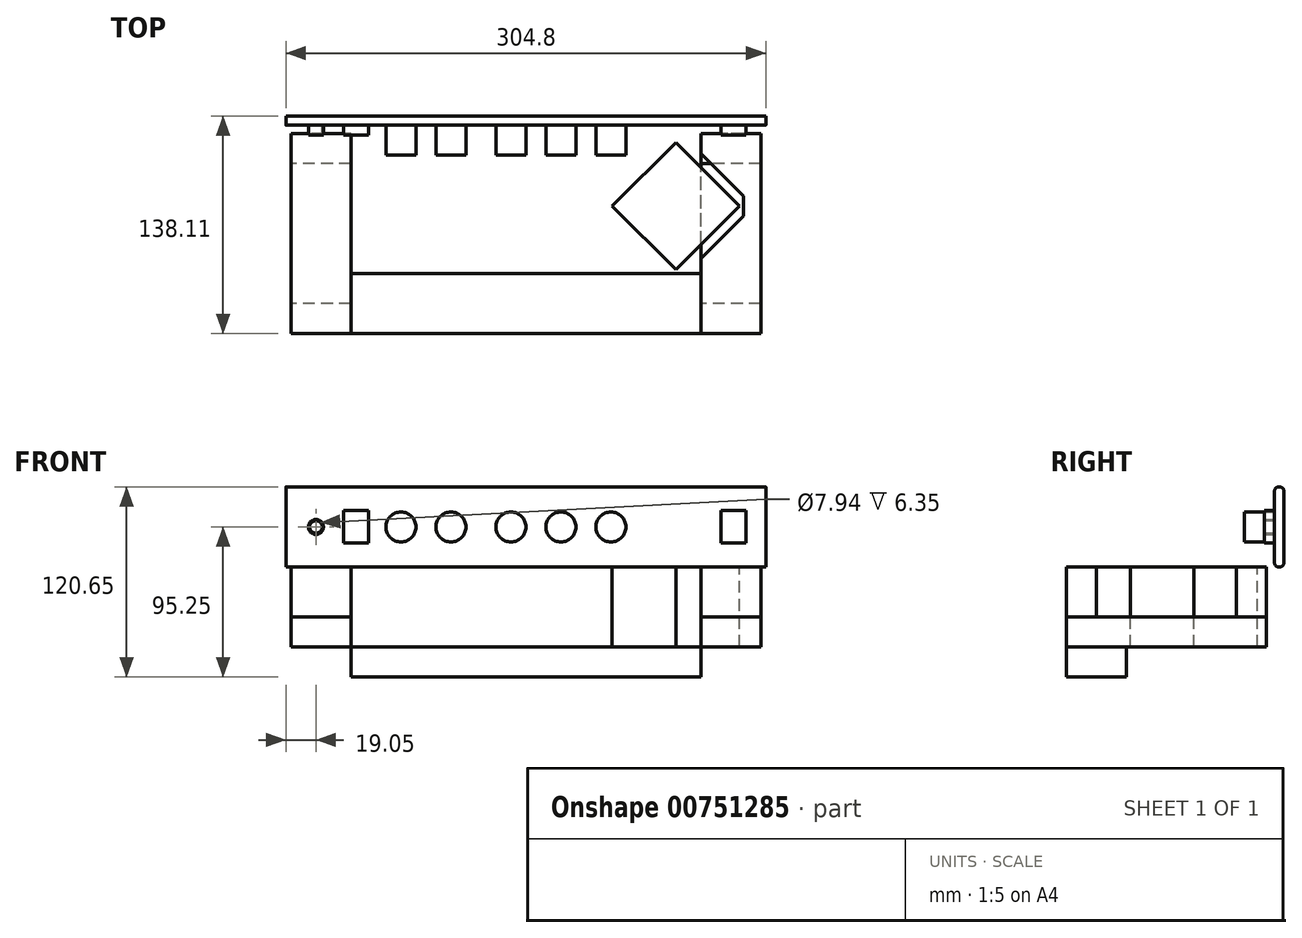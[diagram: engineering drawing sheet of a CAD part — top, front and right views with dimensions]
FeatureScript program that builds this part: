
annotation { "Feature Type Name" : "Feature", "Feature Type Description" : "" }
export const myFeature = defineFeature(function(context is Context, id is Id, definition is map)
    precondition{}
    {
        {
            var Q0;
            Q0=qCreatedBy(makeId("Front.planeOp"),FACE);
            var sketch = newSketch(context, id + "F0", { "sketchPlane" : qUnion([Q0])});
            skLineSegment(sketch, "E0.bottom", {"start": v(152.4, 25.4) * mm, "end": v(-152.4, 25.4) * mm});
            skLineSegment(sketch, "E0.top", {"start": v(152.4, -25.4) * mm, "end": v(-152.4, -25.4) * mm});
            skLineSegment(sketch, "E0.left", {"start": v(152.4, 25.4) * mm, "end": v(152.4, -25.4) * mm});
            skLineSegment(sketch, "E0.right", {"start": v(-152.4, 25.4) * mm, "end": v(-152.4, -25.4) * mm});
            skPoint(sketch, "E0.middle", {"position": v(0, 0) * mm});
            skSolve(sketch);
        }
        {
            var Q0;
            Q0=makeQuery(id+"F0.imprint","IMPRINT",FACE,{"disambiguationData":[TD([[makeQuery(id+"F0.imprint","IMPRINT",EDGE,{"derivedFrom":sQuery(id+"F0.wireOp",EDGE,"E0.bottom")}),1.0]])]});
            extrude(context, id + "F1", {"entities" : qUnion([Q0]), "depth" : (5 + (7 / 8)) * mm, "offsetDistance" : 25.4 * mm});
        }
        {
            var Q0;
            Q0=makeQuery(id+"F1.opExtrude","CAP_FACE",FACE,{"disambiguationData":[OSD([sQuery(id+"F0.wireOp",EDGE,"E0.bottom"),sQuery(id+"F0.wireOp",EDGE,"E0.top"),sQuery(id+"F0.wireOp",EDGE,"E0.left"),sQuery(id+"F0.wireOp",EDGE,"E0.right")])],"isStart":false});
            cPlane(context, id + "F2", {"entities" : qUnion([Q0]), "cplaneType" : CPlaneType.OFFSET, "offset" : 0 * mm, "width" : 152.4 * mm, "height" : 152.4 * mm});
        }
        {
            var Q0;
            Q0=qCreatedBy(id+"F2.planeOp",FACE);
            var sketch = newSketch(context, id + "F3", { "sketchPlane" : qUnion([Q0])});
            skCircle(sketch, "E1", {"center": v(-133.35, 0) * mm, "radius": 4.76 * mm});
            skCircle(sketch, "E2", {"center": v(-133.35, 0) * mm, "radius": 3.97 * mm});
            skLineSegment(sketch, "E3.bottom", {"start": v(-100.01, 10.32) * mm, "end": v(-115.89, 10.32) * mm});
            skLineSegment(sketch, "E3.top", {"start": v(-100.01, -10.32) * mm, "end": v(-115.89, -10.32) * mm});
            skLineSegment(sketch, "E3.left", {"start": v(-100.01, 10.32) * mm, "end": v(-100.01, -10.32) * mm});
            skLineSegment(sketch, "E3.right", {"start": v(-115.89, 10.32) * mm, "end": v(-115.89, -10.32) * mm});
            skPoint(sketch, "E3.middle", {"position": v(-107.95, 0) * mm});
            skLineSegment(sketch, "E4.bottom", {"start": v(139.7, 10.32) * mm, "end": v(123.83, 10.32) * mm});
            skLineSegment(sketch, "E4.top", {"start": v(139.7, -10.32) * mm, "end": v(123.83, -10.32) * mm});
            skLineSegment(sketch, "E4.left", {"start": v(139.7, 10.32) * mm, "end": v(139.7, -10.32) * mm});
            skLineSegment(sketch, "E4.right", {"start": v(123.83, 10.32) * mm, "end": v(123.83, -10.32) * mm});
            skPoint(sketch, "E4.middle", {"position": v(131.76, 0) * mm});
            skSolve(sketch);
        }
        {
            var Q0;
            Q0=qSketchRegion(id+"F3",true);
            extrude(context, id + "F4", {"entities" : qUnion([Q0]), "operationType" : NewBodyOperationType.ADD, "depth" : 6.35 * mm, "offsetDistance" : 25.4 * mm});
        }
        {
            var Q0;
            Q0=qCreatedBy(id+"F2.planeOp",FACE);
            var sketch = newSketch(context, id + "F5", { "sketchPlane" : qUnion([Q0])});
            skCircle(sketch, "E5", {"center": v(-79.38, 0) * mm, "radius": 9.53 * mm});
            skCircle(sketch, "E6", {"center": v(-47.62, 0) * mm, "radius": 9.53 * mm});
            skCircle(sketch, "E7", {"center": v(-9.52, 0) * mm, "radius": 9.53 * mm});
            skCircle(sketch, "E8", {"center": v(22.23, 0) * mm, "radius": 9.53 * mm});
            skCircle(sketch, "E9", {"center": v(53.98, 0) * mm, "radius": 9.53 * mm});
            skSolve(sketch);
        }
        {
            var Q0;
            Q0=makeQuery(id+"F5.imprint","IMPRINT",FACE,{"disambiguationData":[TD([[makeQuery(id+"F5.imprint","IMPRINT",EDGE,{"derivedFrom":sQuery(id+"F5.wireOp",EDGE,"E5")}),1.0]])]});
            var Q1;
            Q1=makeQuery(id+"F5.imprint","IMPRINT",FACE,{"disambiguationData":[TD([[makeQuery(id+"F5.imprint","IMPRINT",EDGE,{"derivedFrom":sQuery(id+"F5.wireOp",EDGE,"E6")}),1.0]])]});
            var Q2;
            Q2=makeQuery(id+"F5.imprint","IMPRINT",FACE,{"disambiguationData":[TD([[makeQuery(id+"F5.imprint","IMPRINT",EDGE,{"derivedFrom":sQuery(id+"F5.wireOp",EDGE,"E7")}),1.0]])]});
            var Q3;
            Q3=makeQuery(id+"F5.imprint","IMPRINT",FACE,{"disambiguationData":[TD([[makeQuery(id+"F5.imprint","IMPRINT",EDGE,{"derivedFrom":sQuery(id+"F5.wireOp",EDGE,"E8")}),1.0]])]});
            var Q4;
            Q4=makeQuery(id+"F5.imprint","IMPRINT",FACE,{"disambiguationData":[TD([[makeQuery(id+"F5.imprint","IMPRINT",EDGE,{"derivedFrom":sQuery(id+"F5.wireOp",EDGE,"E9")}),1.0]])]});
            extrude(context, id + "F6", {"entities" : qUnion([Q0, Q1, Q2, Q3, Q4]), "operationType" : NewBodyOperationType.ADD, "depth" : 19.05 * mm, "offsetDistance" : 25.4 * mm});
        }
        {
            var Q0;
            Q0=makeQuery(id+"F1.opExtrude","SWEPT_FACE",FACE,{"disambiguationData":[OSD([sQuery(id+"F0.wireOp",EDGE,"E0.top")])]});
            cPlane(context, id + "F7", {"entities" : qUnion([Q0]), "cplaneType" : CPlaneType.OFFSET, "offset" : 0 * mm, "width" : 152.4 * mm, "height" : 152.4 * mm});
        }
        {
            var Q0;
            Q0=qCreatedBy(id+"F7.planeOp",FACE);
            var sketch = newSketch(context, id + "F8", { "sketchPlane" : qUnion([Q0])});
            skLineSegment(sketch, "E10.bottom", {"start": v(95.25, 16.74) * mm, "end": v(54.84, 57.15) * mm});
            skLineSegment(sketch, "E10.top", {"start": v(135.66, 57.15) * mm, "end": v(95.25, 97.56) * mm});
            skLineSegment(sketch, "E10.left", {"start": v(95.25, 16.74) * mm, "end": v(135.66, 57.15) * mm});
            skLineSegment(sketch, "E10.right", {"start": v(54.84, 57.15) * mm, "end": v(95.25, 97.56) * mm});
            skPoint(sketch, "E10.middle", {"position": v(95.25, 57.15) * mm});
            skLineSegment(sketch, "E11", {"start": v(3.18, 0) * mm, "end": v(152.4, 149.23) * mm, "construction": true});
            skSolve(sketch);
        }
        {
            var Q0;
            Q0=makeQuery(id+"F8.imprint","IMPRINT",FACE,{"disambiguationData":[TD([[makeQuery(id+"F8.imprint","IMPRINT",EDGE,{"derivedFrom":sQuery(id+"F8.wireOp",EDGE,"E10.bottom")}),-1.0]])]});
            extrude(context, id + "F9", {"entities" : qUnion([Q0]), "operationType" : NewBodyOperationType.ADD, "depth" : 50.8 * mm, "offsetDistance" : 25.4 * mm});
        }
        {
            var Q0;
            Q0=makeQuery(id+"F1.opExtrude","CAP_EDGE",EDGE,{"disambiguationData":[OSD([sQuery(id+"F0.wireOp",EDGE,"E0.bottom")])],"isStart":false});
            var Q1;
            Q1=makeQuery(id+"F1.opExtrude","CAP_EDGE",EDGE,{"disambiguationData":[OSD([sQuery(id+"F0.wireOp",EDGE,"E0.top")])],"isStart":false});
            var Q2;
            Q2=makeQuery(id+"F1.opExtrude","CAP_EDGE",EDGE,{"disambiguationData":[OSD([sQuery(id+"F0.wireOp",EDGE,"E0.bottom")])],"isStart":true});
            var Q3;
            Q3=makeQuery(id+"F1.opExtrude","CAP_EDGE",EDGE,{"disambiguationData":[OSD([sQuery(id+"F0.wireOp",EDGE,"E0.top")])],"isStart":true});
            fillet(context, id + "F10", {"entities" : qUnion([Q0, Q1, Q2, Q3]), "radius" : 2.54 * mm, "tangentPropagation" : true, "allowEdgeOverflow" : false});
        }
        {
            var Q0;
            Q0=qCreatedBy(id+"F7.planeOp",FACE);
            var sketch = newSketch(context, id + "F11", { "sketchPlane" : qUnion([Q0])});
            skLineSegment(sketch, "E12.bottom", {"start": v(-111.13, 11.11) * mm, "end": v(-149.23, 11.11) * mm});
            skLineSegment(sketch, "E12.top", {"start": v(-111.12, 138.11) * mm, "end": v(-149.22, 138.11) * mm});
            skLineSegment(sketch, "E12.left", {"start": v(-111.13, 11.11) * mm, "end": v(-111.12, 138.11) * mm});
            skLineSegment(sketch, "E12.right", {"start": v(-149.23, 11.11) * mm, "end": v(-149.22, 138.11) * mm});
            skPoint(sketch, "E12.middle", {"position": v(-130.18, 74.61) * mm});
            skLineSegment(sketch, "E13", {"start": v(149.22, 138.11) * mm, "end": v(149.22, 11.11) * mm});
            skLineSegment(sketch, "E14", {"start": v(149.22, 11.11) * mm, "end": v(111.13, 11.11) * mm});
            skLineSegment(sketch, "E15", {"start": v(111.12, 11.11) * mm, "end": v(111.12, 23.81) * mm});
            skLineSegment(sketch, "E16", {"start": v(111.12, 23.81) * mm, "end": v(138.11, 50.8) * mm});
            skLineSegment(sketch, "E17", {"start": v(138.11, 50.8) * mm, "end": v(138.11, 63.5) * mm});
            skLineSegment(sketch, "E18", {"start": v(138.11, 63.5) * mm, "end": v(111.12, 90.49) * mm});
            skLineSegment(sketch, "E19", {"start": v(111.12, 90.49) * mm, "end": v(111.12, 138.11) * mm});
            skLineSegment(sketch, "E20", {"start": v(111.12, 138.11) * mm, "end": v(149.22, 138.11) * mm});
            skSolve(sketch);
        }
        {
            var Q0;
            Q0 = qSketchRegion(id + "F11", true);
            extrude(context, id + "F12", {"entities" : qUnion([Q0]), "depth" : 3 / 101.6 * mm, "offsetDistance" : 25.4 * mm});
        }
        {
            var Q0;
            Q0=makeQuery(id+"F12.opExtrude","CAP_FACE",FACE,{"disambiguationData":[OSD([sQuery(id+"F11.wireOp",EDGE,"E12.bottom"),sQuery(id+"F11.wireOp",EDGE,"E12.top"),sQuery(id+"F11.wireOp",EDGE,"E12.left"),sQuery(id+"F11.wireOp",EDGE,"E12.right")])],"isStart":false});
            cPlane(context, id + "F13", {"entities" : qUnion([Q0]), "cplaneType" : CPlaneType.OFFSET, "offset" : 0 * mm, "width" : 152.4 * mm, "height" : 152.4 * mm});
        }
        {
            var Q0;
            Q0=qCreatedBy(id+"F13.planeOp",FACE);
            var sketch = newSketch(context, id + "F14", { "sketchPlane" : qUnion([Q0])});
            skLineSegment(sketch, "E21.bottom", {"start": v(-111.12, 138.11) * mm, "end": v(-149.22, 138.11) * mm});
            skLineSegment(sketch, "E21.top", {"start": v(-111.12, 119.06) * mm, "end": v(-149.22, 119.06) * mm});
            skLineSegment(sketch, "E21.left", {"start": v(-111.12, 138.11) * mm, "end": v(-111.12, 119.06) * mm});
            skLineSegment(sketch, "E21.right", {"start": v(-149.22, 138.11) * mm, "end": v(-149.22, 119.06) * mm});
            skPoint(sketch, "E21.middle", {"position": v(-130.17, 128.59) * mm});
            skLineSegment(sketch, "E22.bottom", {"start": v(-111.13, 30.16) * mm, "end": v(-149.23, 30.16) * mm});
            skLineSegment(sketch, "E22.top", {"start": v(-111.13, 11.11) * mm, "end": v(-149.23, 11.11) * mm});
            skLineSegment(sketch, "E22.left", {"start": v(-111.13, 30.16) * mm, "end": v(-111.13, 11.11) * mm});
            skLineSegment(sketch, "E22.right", {"start": v(-149.23, 30.16) * mm, "end": v(-149.23, 11.11) * mm});
            skPoint(sketch, "E22.middle", {"position": v(-130.18, 20.64) * mm});
            skLineSegment(sketch, "E23.bottom", {"start": v(149.22, 138.11) * mm, "end": v(111.12, 138.11) * mm});
            skLineSegment(sketch, "E23.top", {"start": v(149.22, 119.06) * mm, "end": v(111.12, 119.06) * mm});
            skLineSegment(sketch, "E23.left", {"start": v(149.22, 138.11) * mm, "end": v(149.22, 119.06) * mm});
            skLineSegment(sketch, "E23.right", {"start": v(111.12, 138.11) * mm, "end": v(111.12, 119.06) * mm});
            skPoint(sketch, "E23.middle", {"position": v(130.17, 128.59) * mm});
            skLineSegment(sketch, "E24.bottom", {"start": v(149.22, 30.16) * mm, "end": v(111.13, 30.16) * mm});
            skLineSegment(sketch, "E24.top", {"start": v(149.22, 11.11) * mm, "end": v(111.13, 11.11) * mm});
            skLineSegment(sketch, "E24.left", {"start": v(149.22, 30.16) * mm, "end": v(149.22, 11.11) * mm});
            skLineSegment(sketch, "E24.right", {"start": v(111.13, 30.16) * mm, "end": v(111.13, 11.11) * mm});
            skPoint(sketch, "E24.middle", {"position": v(130.18, 20.64) * mm});
            skSolve(sketch);
        }
        {
            var Q0;
            Q0 = qSketchRegion(id + "F14", true);
            extrude(context, id + "F15", {"entities" : qUnion([Q0]), "depth" : 31.75 * mm, "offsetDistance" : 25.4 * mm});
        }
        {
            var Q0;
            Q0=makeQuery(id+"F15.opExtrude","CAP_FACE",FACE,{"disambiguationData":[OSD([sQuery(id+"F14.wireOp",EDGE,"E24.bottom"),sQuery(id+"F14.wireOp",EDGE,"E24.top"),sQuery(id+"F14.wireOp",EDGE,"E24.left"),sQuery(id+"F14.wireOp",EDGE,"E24.right")])],"isStart":false});
            cPlane(context, id + "F16", {"entities" : qUnion([Q0]), "cplaneType" : CPlaneType.OFFSET, "offset" : 0 * mm, "width" : 152.4 * mm, "height" : 152.4 * mm});
        }
        {
            var Q0;
            Q0=qCreatedBy(id+"F16.planeOp",FACE);
            var sketch = newSketch(context, id + "F17", { "sketchPlane" : qUnion([Q0])});
            skLineSegment(sketch, "E25.bottom", {"start": v(111.12, 138.11) * mm, "end": v(149.22, 138.11) * mm});
            skLineSegment(sketch, "E25.top", {"start": v(111.12, 11.11) * mm, "end": v(149.22, 11.11) * mm});
            skLineSegment(sketch, "E25.left", {"start": v(111.12, 138.11) * mm, "end": v(111.12, 11.11) * mm});
            skLineSegment(sketch, "E25.right", {"start": v(149.22, 138.11) * mm, "end": v(149.22, 11.11) * mm});
            skLineSegment(sketch, "E26.bottom", {"start": v(-149.22, 138.11) * mm, "end": v(-111.13, 138.11) * mm});
            skLineSegment(sketch, "E26.top", {"start": v(-149.22, 11.11) * mm, "end": v(-111.13, 11.11) * mm});
            skLineSegment(sketch, "E26.left", {"start": v(-149.22, 138.11) * mm, "end": v(-149.22, 11.11) * mm});
            skLineSegment(sketch, "E26.right", {"start": v(-111.13, 138.11) * mm, "end": v(-111.13, 11.11) * mm});
            skSolve(sketch);
        }
        {
            var Q0;
            Q0 = qSketchRegion(id + "F17", true);
            extrude(context, id + "F18", {"entities" : qUnion([Q0]), "depth" : 19.05 * mm, "offsetDistance" : 25.4 * mm});
        }
        {
            var Q0;
            Q0=makeQuery(id+"F18.boolean.opBoolean","MERGE",FACE,{"derivedFrom":[makeQuery(id+"F15.boolean.opBoolean","MERGE",FACE,{"derivedFrom":[makeQuery(id+"F12.opExtrude","SWEPT_FACE",FACE,{"disambiguationData":[OSD([sQuery(id+"F11.wireOp",EDGE,"E15")])]}),makeQuery(id+"F15.opExtrude","SWEPT_FACE",FACE,{"disambiguationData":[OSD([sQuery(id+"F14.wireOp",EDGE,"E24.right")])]})]}),makeQuery(id+"F15.boolean.opBoolean","MERGE",FACE,{"derivedFrom":[makeQuery(id+"F12.opExtrude","SWEPT_FACE",FACE,{"disambiguationData":[OSD([sQuery(id+"F11.wireOp",EDGE,"E19")])]}),makeQuery(id+"F15.opExtrude","SWEPT_FACE",FACE,{"disambiguationData":[OSD([sQuery(id+"F14.wireOp",EDGE,"E23.right")])]})]}),makeQuery(id+"F18.opExtrude","SWEPT_FACE",FACE,{"disambiguationData":[OSD([sQuery(id+"F17.wireOp",EDGE,"E25.left")])]})]});
            var sketch = newSketch(context, id + "F19", { "sketchPlane" : qUnion([Q0])});
            skLineSegment(sketch, "E27.bottom", {"start": v(100.01, -76.2) * mm, "end": v(138.11, -76.2) * mm});
            skLineSegment(sketch, "E27.top", {"start": v(100.01, -95.25) * mm, "end": v(138.11, -95.25) * mm});
            skLineSegment(sketch, "E27.left", {"start": v(100.01, -76.2) * mm, "end": v(100.01, -95.25) * mm});
            skLineSegment(sketch, "E27.right", {"start": v(138.11, -76.2) * mm, "end": v(138.11, -95.25) * mm});
            skSolve(sketch);
        }
        {
            var Q0;
            Q0 = qSketchRegion(id + "F19", true);
            extrude(context, id + "F20", {"entities" : qUnion([Q0]), "depth" : 222.25 * mm, "offsetDistance" : 25.4 * mm});
        }
    });
